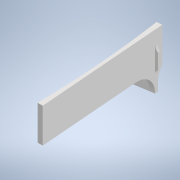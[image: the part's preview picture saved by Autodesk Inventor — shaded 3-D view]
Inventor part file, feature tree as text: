
AUTODESK INVENTOR PART (.ipt)
format: ipt  version: 2020.3 (Build 243373000, 373)  size: 210,944 bytes
history: native  units: mm
features: other x7, extrude x6, sketch x6, fillet x5, reference x5, plane x1, projected_geometry x1
ambient origin geometry x8: Origin, YZ Plane, XZ Plane, XY Plane, X Axis, Y Axis, Z Axis, Center Point
bodies: Solid1 (feature_tree)
feature tree (31):
  other  "Blocks"
  extrude  "Extrusion1"  Depth=5.0mm
  extrude  "Extrusion2"  Depth=2.5mm
  extrude  "Extrusion3"  Depth=5.0mm
  fillet  "Fillet1"  Radius=2.5mm
  fillet  "Fillet2"  Radius=5.0mm
  fillet  "Fillet3"  Radius=20.0mm
  fillet  "Fillet4"  Radius=3.25mm
  sketch  "Sketch4"  dims[d14=20.0mm d15=20.0mm]
  plane  "Work Plane1"
  extrude  "Extrusion4"  Depth=20.0mm
  extrude  "Extrusion5"  Depth=1.5mm TaperAngle=0.0deg
  extrude  "Extrusion6"  Depth=10.0mm TaperAngle=0.0deg
  fillet  "Fillet5"  Radius=1.75mm
  sketch  "Sketch1"  dims[d1=5.0mm d2=5.0mm]
  other  "Arc"
  sketch  "Sketch2"  dims[d3=33.0mm d4=0.0mm d5=2.5mm]
  sketch  "Sketch3"  dims[d6=15.0mm d7=5.0mm d8=2.5mm d9=0.0mm d10=5.0mm d11=20.0mm d12=0.0mm d13=3.25mm]
  reference  "Reference1"
  reference  "Reference2"
  sketch  "Sketch5"  dims[d16=7.25mm d17=1.5mm d18=0.0mm]
  reference  "Reference3"
  reference  "Reference4"
  reference  "Reference5"
  sketch  "Sketch6"  dims[d19=10.0mm d20=0.0mm d21=10.0mm d22=0.0mm d23=1.75mm]
  projected_geometry  "Projected Loop1"
  other  "Arc:1"
  other  "<userpath>\Documents\Inventor\TheArch\R&D\Beta0\Structura\Prototip\Prototip1.iam"
  other  "Prototip1.iam"
  other  "MG996:3"
  other  "PrindereDisc:1"
